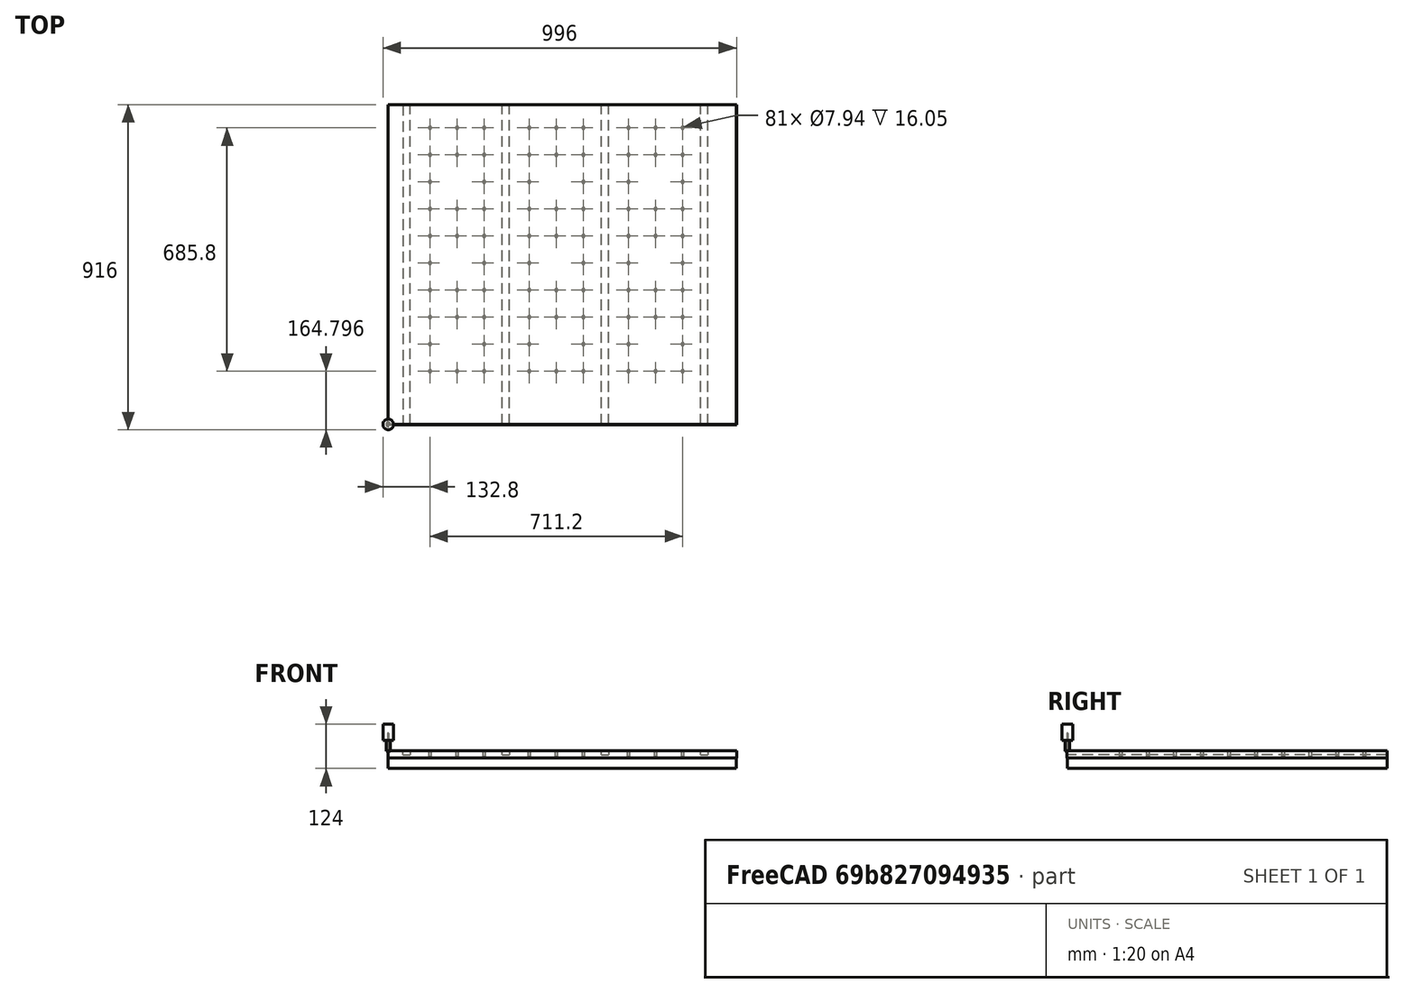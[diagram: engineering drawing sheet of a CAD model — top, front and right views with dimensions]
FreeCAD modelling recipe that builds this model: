
FCSTD DOCUMENT  (FreeCAD 0.21R33771 (Git))
Label: test
License: All rights reserved
LicenseURL: https://en.wikipedia.org/wiki/All_rights_reserved
objects: Part::FeaturePython×13, Path::FeaturePython×12, App::DocumentObjectGroup×9, Sketcher::SketchObject×3, Part::Extrusion×3, App::FeaturePython×3, Part::Cut×2, Part::Box×1, Mesh::FeaturePython×1, Part::MultiCommon×1, App::Part×1
note: 28 computed .brp shape members not serialized (recipe doc carries the construction recipe); baked Part::Feature solids carry a one-line shape summary decoded from their .brp

FEATURE [Sketcher::SketchObject] Sketch
  FullyConstrained = true
  MapMode = 5
  Placement = pos=(0,0,0) rot=(1,0,0;1.5708rad)
  Support = -> [XZ_Plane]
  sketch-geometry (8):
    g0: LineSegment StartX=0 StartY=0 StartZ=0 EndX=1219.2 EndY=0 EndZ=0
    g1: LineSegment StartX=1219.2 StartY=0 StartZ=0 EndX=1219.2 EndY=-12.7 EndZ=0
    g2: LineSegment StartX=1219.2 StartY=-12.7 StartZ=0 EndX=1193.8 EndY=-12.7 EndZ=0
    g3: LineSegment StartX=1193.8 StartY=-12.7 StartZ=0 EndX=1193.8 EndY=-19.05 EndZ=0
    g4: LineSegment StartX=1193.8 StartY=-19.05 StartZ=0 EndX=25.4 EndY=-19.05 EndZ=0
    g5: LineSegment StartX=0 StartY=0 StartZ=0 EndX=0 EndY=-12.7 EndZ=0
    g6: LineSegment StartX=0 StartY=-12.7 StartZ=0 EndX=25.4 EndY=-12.7 EndZ=0
    g7: LineSegment StartX=25.4 StartY=-19.05 StartZ=0 EndX=25.4 EndY=-12.7 EndZ=0
  constraints (23):
    c: Horizontal(g0)
    c: Coincident(g1,g0)
    c: Vertical(g1)
    c: Coincident(g2,g1)
    c: Horizontal(g2)
    c: Coincident(g3,g2)
    c: Vertical(g3)
    c: Coincident(g4,g3)
    c: Horizontal(g4)
    c: Coincident(g5,g0)
    c: Coincident(g6,g5)
    c: Horizontal(g6)
    c: Coincident(g7,g4)
    c: Coincident(g7,g6)
    c: Vertical(g7)
    c: Equal(g1,g5)
    c: Vertical(g5)
    c: Coincident(g0,g-1)
    c: DistanceX(g0,g0) = 1219.2
    c: DistanceX(g4,g4) = 1168.4
    c: DistanceY(g4,g0) = 19.05
    c: DistanceY(g5,g5) = 12.7
    c: DistanceX(g6,g6) = 25.4
FEATURE [Part::Extrusion] Extrude
  Base = -> Sketch
  Dir = (0,-1,2e-16)
  DirMode = 2
  FaceMakerClass = Part::FaceMakerBullseye
  LengthFwd = 1219.2
  LengthRev = 0
  Solid = true
  Symmetric = false
FEATURE [Sketcher::SketchObject] Sketch001
  FullyConstrained = true
  MapMode = 5
  Support = -> [Extrude]
  sketch-geometry (203):
    g0: Circle CenterX=254 CenterY=-152.4 CenterZ=0 NormalX=0 NormalY=0 NormalZ=1 AngleXU=0 Radius=3.96875
    g1: Circle CenterX=330.2 CenterY=-152.4 CenterZ=0 NormalX=0 NormalY=0 NormalZ=1 AngleXU=0 Radius=3.96875
    g2: LineSegment StartX=254 StartY=-152.4 StartZ=0 EndX=330.2 EndY=-152.4 EndZ=0
    g3: Circle CenterX=406.4 CenterY=-152.4 CenterZ=0 NormalX=0 NormalY=0 NormalZ=1 AngleXU=0 Radius=3.96875
    g4: LineSegment StartX=330.2 StartY=-152.4 StartZ=0 EndX=406.4 EndY=-152.4 EndZ=0
    g5: Circle CenterX=254 CenterY=-228.6 CenterZ=0 NormalX=0 NormalY=0 NormalZ=1 AngleXU=0 Radius=3.96875
    g6: LineSegment StartX=254 StartY=-152.4 StartZ=0 EndX=254 EndY=-228.6 EndZ=0
    g7: LineSegment StartX=254 StartY=-228.6 StartZ=0 EndX=330.2 EndY=-228.6 EndZ=0
    g8: Circle CenterX=406.4 CenterY=-228.6 CenterZ=0 NormalX=0 NormalY=0 NormalZ=1 AngleXU=0 Radius=3.96875
    g9: LineSegment StartX=330.2 StartY=-228.6 StartZ=0 EndX=406.4 EndY=-228.6 EndZ=0
    g10: Circle CenterX=254 CenterY=-304.8 CenterZ=0 NormalX=0 NormalY=0 NormalZ=1 AngleXU=0 Radius=3.96875
    g11: LineSegment StartX=254 StartY=-228.6 StartZ=0 EndX=254 EndY=-304.8 EndZ=0
    g12: Circle CenterX=330.2 CenterY=-304.8 CenterZ=0 NormalX=0 NormalY=0 NormalZ=1 AngleXU=0 Radius=3.96875
    g13: LineSegment StartX=254 StartY=-304.8 StartZ=0 EndX=330.2 EndY=-304.8 EndZ=0
    g14: Circle CenterX=406.4 CenterY=-304.8 CenterZ=0 NormalX=0 NormalY=0 NormalZ=1 AngleXU=0 Radius=3.96875
    g15: LineSegment StartX=330.2 StartY=-304.8 StartZ=0 EndX=406.4 EndY=-304.8 EndZ=0
    g16: Circle CenterX=254 CenterY=-381 CenterZ=0 NormalX=0 NormalY=0 NormalZ=1 AngleXU=0 Radius=3.96875
    g17: Circle CenterX=330.2 CenterY=-381 CenterZ=0 NormalX=0 NormalY=0 NormalZ=1 AngleXU=0 Radius=3.96875
    g18: LineSegment StartX=254 StartY=-381 StartZ=0 EndX=330.2 EndY=-381 EndZ=0
    g19: Circle CenterX=406.4 CenterY=-381 CenterZ=0 NormalX=0 NormalY=0 NormalZ=1 AngleXU=0 Radius=3.96875
    g20: LineSegment StartX=330.2 StartY=-381 StartZ=0 EndX=406.4 EndY=-381 EndZ=0
    g21: Circle CenterX=254 CenterY=-457.2 CenterZ=0 NormalX=0 NormalY=0 NormalZ=1 AngleXU=0 Radius=3.96875
    g22: LineSegment StartX=254 StartY=-381 StartZ=0 EndX=254 EndY=-457.2 EndZ=0
    g23: LineSegment StartX=254 StartY=-457.2 StartZ=0 EndX=330.2 EndY=-457.2 EndZ=0
    g24: Circle CenterX=406.4 CenterY=-457.2 CenterZ=0 NormalX=0 NormalY=0 NormalZ=1 AngleXU=0 Radius=3.96875
    g25: LineSegment StartX=330.2 StartY=-457.2 StartZ=0 EndX=406.4 EndY=-457.2 EndZ=0
    g26: Circle CenterX=254 CenterY=-533.4 CenterZ=0 NormalX=0 NormalY=0 NormalZ=1 AngleXU=0 Radius=3.96875
    g27: LineSegment StartX=254 StartY=-457.2 StartZ=0 EndX=254 EndY=-533.4 EndZ=0
    g28: Circle CenterX=330.2 CenterY=-533.4 CenterZ=0 NormalX=0 NormalY=0 NormalZ=1 AngleXU=0 Radius=3.96875
    g29: LineSegment StartX=254 StartY=-533.4 StartZ=0 EndX=330.2 EndY=-533.4 EndZ=0
    g30: Circle CenterX=406.4 CenterY=-533.4 CenterZ=0 NormalX=0 NormalY=0 NormalZ=1 AngleXU=0 Radius=3.96875
    g31: LineSegment StartX=330.2 StartY=-533.4 StartZ=0 EndX=406.4 EndY=-533.4 EndZ=0
    g32: LineSegment StartX=254 StartY=-152.4 StartZ=0 EndX=254 EndY=-381 EndZ=0
    g33: Circle CenterX=254 CenterY=-609.6 CenterZ=0 NormalX=0 NormalY=0 NormalZ=1 AngleXU=0 Radius=3.96875
    g34: Circle CenterX=330.2 CenterY=-609.6 CenterZ=0 NormalX=0 NormalY=0 NormalZ=1 AngleXU=0 Radius=3.96875
    g35: LineSegment StartX=254 StartY=-609.6 StartZ=0 EndX=330.2 EndY=-609.6 EndZ=0
    g36: Circle CenterX=406.4 CenterY=-609.6 CenterZ=0 NormalX=0 NormalY=0 NormalZ=1 AngleXU=0 Radius=3.96875
    g37: LineSegment StartX=330.2 StartY=-609.6 StartZ=0 EndX=406.4 EndY=-609.6 EndZ=0
    g38: Circle CenterX=254 CenterY=-685.8 CenterZ=0 NormalX=0 NormalY=0 NormalZ=1 AngleXU=0 Radius=3.96875
    g39: LineSegment StartX=254 StartY=-609.6 StartZ=0 EndX=254 EndY=-685.8 EndZ=0
    g40: LineSegment StartX=254 StartY=-685.8 StartZ=0 EndX=330.2 EndY=-685.8 EndZ=0
    g41: Circle CenterX=406.4 CenterY=-685.8 CenterZ=0 NormalX=0 NormalY=0 NormalZ=1 AngleXU=0 Radius=3.96875
    g42: LineSegment StartX=330.2 StartY=-685.8 StartZ=0 EndX=406.4 EndY=-685.8 EndZ=0
    g43: Circle CenterX=254 CenterY=-762 CenterZ=0 NormalX=0 NormalY=0 NormalZ=1 AngleXU=0 Radius=3.96875
    g44: LineSegment StartX=254 StartY=-685.8 StartZ=0 EndX=254 EndY=-762 EndZ=0
    g45: Circle CenterX=330.2 CenterY=-762 CenterZ=0 NormalX=0 NormalY=0 NormalZ=1 AngleXU=0 Radius=3.96875
    g46: LineSegment StartX=254 StartY=-762 StartZ=0 EndX=330.2 EndY=-762 EndZ=0
    g47: Circle CenterX=406.4 CenterY=-762 CenterZ=0 NormalX=0 NormalY=0 NormalZ=1 AngleXU=0 Radius=3.96875
    g48: LineSegment StartX=330.2 StartY=-762 StartZ=0 EndX=406.4 EndY=-762 EndZ=0
    g49: LineSegment StartX=254 StartY=-381 StartZ=0 EndX=254 EndY=-609.6 EndZ=0
    g50: Circle CenterX=254 CenterY=-838.2 CenterZ=0 NormalX=0 NormalY=0 NormalZ=1 AngleXU=0 Radius=3.96875
    g51: Circle CenterX=330.2 CenterY=-838.2 CenterZ=0 NormalX=0 NormalY=0 NormalZ=1 AngleXU=0 Radius=3.96875
    g52: LineSegment StartX=254 StartY=-838.2 StartZ=0 EndX=330.2 EndY=-838.2 EndZ=0
    g53: Circle CenterX=406.4 CenterY=-838.2 CenterZ=0 NormalX=0 NormalY=0 NormalZ=1 AngleXU=0 Radius=3.96875
    g54: LineSegment StartX=330.2 StartY=-838.2 StartZ=0 EndX=406.4 EndY=-838.2 EndZ=0
    g55: Circle CenterX=254 CenterY=-914.4 CenterZ=0 NormalX=0 NormalY=0 NormalZ=1 AngleXU=0 Radius=3.96875
    g56: LineSegment StartX=254 StartY=-838.2 StartZ=0 EndX=254 EndY=-914.4 EndZ=0
    g57: LineSegment StartX=254 StartY=-914.4 StartZ=0 EndX=330.2 EndY=-914.4 EndZ=0
    g58: Circle CenterX=406.4 CenterY=-914.4 CenterZ=0 NormalX=0 NormalY=0 NormalZ=1 AngleXU=0 Radius=3.96875
    g59: LineSegment StartX=330.2 StartY=-914.4 StartZ=0 EndX=406.4 EndY=-914.4 EndZ=0
    g60: Circle CenterX=254 CenterY=-990.6 CenterZ=0 NormalX=0 NormalY=0 NormalZ=1 AngleXU=0 Radius=3.96875
    g61: LineSegment StartX=254 StartY=-914.4 StartZ=0 EndX=254 EndY=-990.6 EndZ=0
    g62: Circle CenterX=330.2 CenterY=-990.6 CenterZ=0 NormalX=0 NormalY=0 NormalZ=1 AngleXU=0 Radius=3.96875
    g63: LineSegment StartX=254 StartY=-990.6 StartZ=0 EndX=330.2 EndY=-990.6 EndZ=0
    g64: Circle CenterX=406.4 CenterY=-990.6 CenterZ=0 NormalX=0 NormalY=0 NormalZ=1 AngleXU=0 Radius=3.96875
    g65: LineSegment StartX=330.2 StartY=-990.6 StartZ=0 EndX=406.4 EndY=-990.6 EndZ=0
    g66: LineSegment StartX=254 StartY=-609.6 StartZ=0 EndX=254 EndY=-838.2 EndZ=0
    g67: Circle CenterX=533.4 CenterY=-152.4 CenterZ=0 NormalX=0 NormalY=0 NormalZ=1 AngleXU=0 Radius=3.96875
    g68: Circle CenterX=609.6 CenterY=-152.4 CenterZ=0 NormalX=0 NormalY=0 NormalZ=1 AngleXU=0 Radius=3.96875
    g69: LineSegment StartX=533.4 StartY=-152.4 StartZ=0 EndX=609.6 EndY=-152.4 EndZ=0
    g70: Circle CenterX=685.8 CenterY=-152.4 CenterZ=0 NormalX=0 NormalY=0 NormalZ=1 AngleXU=0 Radius=3.96875
    g71: LineSegment StartX=609.6 StartY=-152.4 StartZ=0 EndX=685.8 EndY=-152.4 EndZ=0
    g72: Circle CenterX=533.4 CenterY=-228.6 CenterZ=0 NormalX=0 NormalY=0 NormalZ=1 AngleXU=0 Radius=3.96875
    g73: LineSegment StartX=533.4 StartY=-152.4 StartZ=0 EndX=533.4 EndY=-228.6 EndZ=0
    g74: LineSegment StartX=533.4 StartY=-228.6 StartZ=0 EndX=609.6 EndY=-228.6 EndZ=0
    g75: Circle CenterX=685.8 CenterY=-228.6 CenterZ=0 NormalX=0 NormalY=0 NormalZ=1 AngleXU=0 Radius=3.96875
    g76: LineSegment StartX=609.6 StartY=-228.6 StartZ=0 EndX=685.8 EndY=-228.6 EndZ=0
    g77: Circle CenterX=533.4 CenterY=-304.8 CenterZ=0 NormalX=0 NormalY=0 NormalZ=1 AngleXU=0 Radius=3.96875
    g78: LineSegment StartX=533.4 StartY=-228.6 StartZ=0 EndX=533.4 EndY=-304.8 EndZ=0
    g79: Circle CenterX=609.6 CenterY=-304.8 CenterZ=0 NormalX=0 NormalY=0 NormalZ=1 AngleXU=0 Radius=3.96875
    g80: LineSegment StartX=533.4 StartY=-304.8 StartZ=0 EndX=609.6 EndY=-304.8 EndZ=0
    g81: Circle CenterX=685.8 CenterY=-304.8 CenterZ=0 NormalX=0 NormalY=0 NormalZ=1 AngleXU=0 Radius=3.96875
    g82: LineSegment StartX=609.6 StartY=-304.8 StartZ=0 EndX=685.8 EndY=-304.8 EndZ=0
    g83: Circle CenterX=533.4 CenterY=-381 CenterZ=0 NormalX=0 NormalY=0 NormalZ=1 AngleXU=0 Radius=3.96875
    g84: Circle CenterX=609.6 CenterY=-381 CenterZ=0 NormalX=0 NormalY=0 NormalZ=1 AngleXU=0 Radius=3.96875
    g85: LineSegment StartX=533.4 StartY=-381 StartZ=0 EndX=609.6 EndY=-381 EndZ=0
    g86: Circle CenterX=685.8 CenterY=-381 CenterZ=0 NormalX=0 NormalY=0 NormalZ=1 AngleXU=0 Radius=3.96875
    g87: LineSegment StartX=609.6 StartY=-381 StartZ=0 EndX=685.8 EndY=-381 EndZ=0
    g88: Circle CenterX=533.4 CenterY=-457.2 CenterZ=0 NormalX=0 NormalY=0 NormalZ=1 AngleXU=0 Radius=3.96875
    g89: LineSegment StartX=533.4 StartY=-381 StartZ=0 EndX=533.4 EndY=-457.2 EndZ=0
    g90: LineSegment StartX=533.4 StartY=-457.2 StartZ=0 EndX=609.6 EndY=-457.2 EndZ=0
    g91: Circle CenterX=685.8 CenterY=-457.2 CenterZ=0 NormalX=0 NormalY=0 NormalZ=1 AngleXU=0 Radius=3.96875
    g92: LineSegment StartX=609.6 StartY=-457.2 StartZ=0 EndX=685.8 EndY=-457.2 EndZ=0
    g93: Circle CenterX=533.4 CenterY=-533.4 CenterZ=0 NormalX=0 NormalY=0 NormalZ=1 AngleXU=0 Radius=3.96875
    g94: LineSegment StartX=533.4 StartY=-457.2 StartZ=0 EndX=533.4 EndY=-533.4 EndZ=0
    g95: Circle CenterX=609.6 CenterY=-533.4 CenterZ=0 NormalX=0 NormalY=0 NormalZ=1 AngleXU=0 Radius=3.96875
    g96: LineSegment StartX=533.4 StartY=-533.4 StartZ=0 EndX=609.6 EndY=-533.4 EndZ=0
    g97: Circle CenterX=685.8 CenterY=-533.4 CenterZ=0 NormalX=0 NormalY=0 NormalZ=1 AngleXU=0 Radius=3.96875
    g98: LineSegment StartX=609.6 StartY=-533.4 StartZ=0 EndX=685.8 EndY=-533.4 EndZ=0
    g99: LineSegment StartX=533.4 StartY=-152.4 StartZ=0 EndX=533.4 EndY=-381 EndZ=0
    g100: Circle CenterX=533.4 CenterY=-609.6 CenterZ=0 NormalX=0 NormalY=0 NormalZ=1 AngleXU=0 Radius=3.96875
    g101: Circle CenterX=609.6 CenterY=-609.6 CenterZ=0 NormalX=0 NormalY=0 NormalZ=1 AngleXU=0 Radius=3.96875
    g102: LineSegment StartX=533.4 StartY=-609.6 StartZ=0 EndX=609.6 EndY=-609.6 EndZ=0
    g103: Circle CenterX=685.8 CenterY=-609.6 CenterZ=0 NormalX=0 NormalY=0 NormalZ=1 AngleXU=0 Radius=3.96875
    g104: LineSegment StartX=609.6 StartY=-609.6 StartZ=0 EndX=685.8 EndY=-609.6 EndZ=0
    g105: Circle CenterX=533.4 CenterY=-685.8 CenterZ=0 NormalX=0 NormalY=0 NormalZ=1 AngleXU=0 Radius=3.96875
    g106: LineSegment StartX=533.4 StartY=-609.6 StartZ=0 EndX=533.4 EndY=-685.8 EndZ=0
    g107: LineSegment StartX=533.4 StartY=-685.8 StartZ=0 EndX=609.6 EndY=-685.8 EndZ=0
    g108: Circle CenterX=685.8 CenterY=-685.8 CenterZ=0 NormalX=0 NormalY=0 NormalZ=1 AngleXU=0 Radius=3.96875
    g109: LineSegment StartX=609.6 StartY=-685.8 StartZ=0 EndX=685.8 EndY=-685.8 EndZ=0
    g110: Circle CenterX=533.4 CenterY=-762 CenterZ=0 NormalX=0 NormalY=0 NormalZ=1 AngleXU=0 Radius=3.96875
    g111: LineSegment StartX=533.4 StartY=-685.8 StartZ=0 EndX=533.4 EndY=-762 EndZ=0
    g112: Circle CenterX=609.6 CenterY=-762 CenterZ=0 NormalX=0 NormalY=0 NormalZ=1 AngleXU=0 Radius=3.96875
    g113: LineSegment StartX=533.4 StartY=-762 StartZ=0 EndX=609.6 EndY=-762 EndZ=0
    g114: Circle CenterX=685.8 CenterY=-762 CenterZ=0 NormalX=0 NormalY=0 NormalZ=1 AngleXU=0 Radius=3.96875
    g115: LineSegment StartX=609.6 StartY=-762 StartZ=0 EndX=685.8 EndY=-762 EndZ=0
    g116: LineSegment StartX=533.4 StartY=-381 StartZ=0 EndX=533.4 EndY=-609.6 EndZ=0
    g117: Circle CenterX=533.4 CenterY=-838.2 CenterZ=0 NormalX=0 NormalY=0 NormalZ=1 AngleXU=0 Radius=3.96875
    g118: Circle CenterX=609.6 CenterY=-838.2 CenterZ=0 NormalX=0 NormalY=0 NormalZ=1 AngleXU=0 Radius=3.96875
    g119: LineSegment StartX=533.4 StartY=-838.2 StartZ=0 EndX=609.6 EndY=-838.2 EndZ=0
    g120: Circle CenterX=685.8 CenterY=-838.2 CenterZ=0 NormalX=0 NormalY=0 NormalZ=1 AngleXU=0 Radius=3.96875
    g121: LineSegment StartX=609.6 StartY=-838.2 StartZ=0 EndX=685.8 EndY=-838.2 EndZ=0
    g122: Circle CenterX=533.4 CenterY=-914.4 CenterZ=0 NormalX=0 NormalY=0 NormalZ=1 AngleXU=0 Radius=3.96875
    g123: LineSegment StartX=533.4 StartY=-838.2 StartZ=0 EndX=533.4 EndY=-914.4 EndZ=0
    g124: LineSegment StartX=533.4 StartY=-914.4 StartZ=0 EndX=609.6 EndY=-914.4 EndZ=0
    g125: Circle CenterX=685.8 CenterY=-914.4 CenterZ=0 NormalX=0 NormalY=0 NormalZ=1 AngleXU=0 Radius=3.96875
    g126: LineSegment StartX=609.6 StartY=-914.4 StartZ=0 EndX=685.8 EndY=-914.4 EndZ=0
    g127: Circle CenterX=533.4 CenterY=-990.6 CenterZ=0 NormalX=0 NormalY=0 NormalZ=1 AngleXU=0 Radius=3.96875
    g128: LineSegment StartX=533.4 StartY=-914.4 StartZ=0 EndX=533.4 EndY=-990.6 EndZ=0
    g129: Circle CenterX=609.6 CenterY=-990.6 CenterZ=0 NormalX=0 NormalY=0 NormalZ=1 AngleXU=0 Radius=3.96875
    g130: LineSegment StartX=533.4 StartY=-990.6 StartZ=0 EndX=609.6 EndY=-990.6 EndZ=0
    g131: Circle CenterX=685.8 CenterY=-990.6 CenterZ=0 NormalX=0 NormalY=0 NormalZ=1 AngleXU=0 Radius=3.96875
    g132: LineSegment StartX=609.6 StartY=-990.6 StartZ=0 EndX=685.8 EndY=-990.6 EndZ=0
    g133: LineSegment StartX=533.4 StartY=-609.6 StartZ=0 EndX=533.4 EndY=-838.2 EndZ=0
    g134: LineSegment StartX=254 StartY=-152.4 StartZ=0 EndX=533.4 EndY=-152.4 EndZ=0
    g135: Circle CenterX=812.8 CenterY=-152.4 CenterZ=0 NormalX=0 NormalY=0 NormalZ=1 AngleXU=0 Radius=3.96875
    g136: Circle CenterX=889 CenterY=-152.4 CenterZ=0 NormalX=0 NormalY=0 NormalZ=1 AngleXU=0 Radius=3.96875
    g137: LineSegment StartX=812.8 StartY=-152.4 StartZ=0 EndX=889 EndY=-152.4 EndZ=0
    g138: Circle CenterX=965.2 CenterY=-152.4 CenterZ=0 NormalX=0 NormalY=0 NormalZ=1 AngleXU=0 Radius=3.96875
    g139: LineSegment StartX=889 StartY=-152.4 StartZ=0 EndX=965.2 EndY=-152.4 EndZ=0
    g140: Circle CenterX=812.8 CenterY=-228.6 CenterZ=0 NormalX=0 NormalY=0 NormalZ=1 AngleXU=0 Radius=3.96875
    g141: LineSegment StartX=812.8 StartY=-152.4 StartZ=0 EndX=812.8 EndY=-228.6 EndZ=0
    g142: LineSegment StartX=812.8 StartY=-228.6 StartZ=0 EndX=889 EndY=-228.6 EndZ=0
    g143: Circle CenterX=965.2 CenterY=-228.6 CenterZ=0 NormalX=0 NormalY=0 NormalZ=1 AngleXU=0 Radius=3.96875
    g144: LineSegment StartX=889 StartY=-228.6 StartZ=0 EndX=965.2 EndY=-228.6 EndZ=0
    g145: Circle CenterX=812.8 CenterY=-304.8 CenterZ=0 NormalX=0 NormalY=0 NormalZ=1 AngleXU=0 Radius=3.96875
    g146: LineSegment StartX=812.8 StartY=-228.6 StartZ=0 EndX=812.8 EndY=-304.8 EndZ=0
    g147: Circle CenterX=889 CenterY=-304.8 CenterZ=0 NormalX=0 NormalY=0 NormalZ=1 AngleXU=0 Radius=3.96875
    g148: LineSegment StartX=812.8 StartY=-304.8 StartZ=0 EndX=889 EndY=-304.8 EndZ=0
    g149: Circle CenterX=965.2 CenterY=-304.8 CenterZ=0 NormalX=0 NormalY=0 NormalZ=1 AngleXU=0 Radius=3.96875
    g150: LineSegment StartX=889 StartY=-304.8 StartZ=0 EndX=965.2 EndY=-304.8 EndZ=0
    g151: Circle CenterX=812.8 CenterY=-381 CenterZ=0 NormalX=0 NormalY=0 NormalZ=1 AngleXU=0 Radius=3.96875
    g152: Circle CenterX=889 CenterY=-381 CenterZ=0 NormalX=0 NormalY=0 NormalZ=1 AngleXU=0 Radius=3.96875
    g153: LineSegment StartX=812.8 StartY=-381 StartZ=0 EndX=889 EndY=-381 EndZ=0
    g154: Circle CenterX=965.2 CenterY=-381 CenterZ=0 NormalX=0 NormalY=0 NormalZ=1 AngleXU=0 Radius=3.96875
    g155: LineSegment StartX=889 StartY=-381 StartZ=0 EndX=965.2 EndY=-381 EndZ=0
    g156: Circle CenterX=812.8 CenterY=-457.2 CenterZ=0 NormalX=0 NormalY=0 NormalZ=1 AngleXU=0 Radius=3.96875
    g157: LineSegment StartX=812.8 StartY=-381 StartZ=0 EndX=812.8 EndY=-457.2 EndZ=0
    g158: LineSegment StartX=812.8 StartY=-457.2 StartZ=0 EndX=889 EndY=-457.2 EndZ=0
    g159: Circle CenterX=965.2 CenterY=-457.2 CenterZ=0 NormalX=0 NormalY=0 NormalZ=1 AngleXU=0 Radius=3.96875
    g160: LineSegment StartX=889 StartY=-457.2 StartZ=0 EndX=965.2 EndY=-457.2 EndZ=0
    g161: Circle CenterX=812.8 CenterY=-533.4 CenterZ=0 NormalX=0 NormalY=0 NormalZ=1 AngleXU=0 Radius=3.96875
    g162: LineSegment StartX=812.8 StartY=-457.2 StartZ=0 EndX=812.8 EndY=-533.4 EndZ=0
    g163: Circle CenterX=889 CenterY=-533.4 CenterZ=0 NormalX=0 NormalY=0 NormalZ=1 AngleXU=0 Radius=3.96875
    g164: LineSegment StartX=812.8 StartY=-533.4 StartZ=0 EndX=889 EndY=-533.4 EndZ=0
    g165: Circle CenterX=965.2 CenterY=-533.4 CenterZ=0 NormalX=0 NormalY=0 NormalZ=1 AngleXU=0 Radius=3.96875
    g166: LineSegment StartX=889 StartY=-533.4 StartZ=0 EndX=965.2 EndY=-533.4 EndZ=0
    g167: LineSegment StartX=812.8 StartY=-152.4 StartZ=0 EndX=812.8 EndY=-381 EndZ=0
    g168: Circle CenterX=812.8 CenterY=-609.6 CenterZ=0 NormalX=0 NormalY=0 NormalZ=1 AngleXU=0 Radius=3.96875
    g169: Circle CenterX=889 CenterY=-609.6 CenterZ=0 NormalX=0 NormalY=0 NormalZ=1 AngleXU=0 Radius=3.96875
    g170: LineSegment StartX=812.8 StartY=-609.6 StartZ=0 EndX=889 EndY=-609.6 EndZ=0
    g171: Circle CenterX=965.2 CenterY=-609.6 CenterZ=0 NormalX=0 NormalY=0 NormalZ=1 AngleXU=0 Radius=3.96875
    g172: LineSegment StartX=889 StartY=-609.6 StartZ=0 EndX=965.2 EndY=-609.6 EndZ=0
    g173: Circle CenterX=812.8 CenterY=-685.8 CenterZ=0 NormalX=0 NormalY=0 NormalZ=1 AngleXU=0 Radius=3.96875
    g174: LineSegment StartX=812.8 StartY=-609.6 StartZ=0 EndX=812.8 EndY=-685.8 EndZ=0
    g175: LineSegment StartX=812.8 StartY=-685.8 StartZ=0 EndX=889 EndY=-685.8 EndZ=0
    g176: Circle CenterX=965.2 CenterY=-685.8 CenterZ=0 NormalX=0 NormalY=0 NormalZ=1 AngleXU=0 Radius=3.96875
    g177: LineSegment StartX=889 StartY=-685.8 StartZ=0 EndX=965.2 EndY=-685.8 EndZ=0
    g178: Circle CenterX=812.8 CenterY=-762 CenterZ=0 NormalX=0 NormalY=0 NormalZ=1 AngleXU=0 Radius=3.96875
    g179: LineSegment StartX=812.8 StartY=-685.8 StartZ=0 EndX=812.8 EndY=-762 EndZ=0
    g180: Circle CenterX=889 CenterY=-762 CenterZ=0 NormalX=0 NormalY=0 NormalZ=1 AngleXU=0 Radius=3.96875
    g181: LineSegment StartX=812.8 StartY=-762 StartZ=0 EndX=889 EndY=-762 EndZ=0
    g182: Circle CenterX=965.2 CenterY=-762 CenterZ=0 NormalX=0 NormalY=0 NormalZ=1 AngleXU=0 Radius=3.96875
    g183: LineSegment StartX=889 StartY=-762 StartZ=0 EndX=965.2 EndY=-762 EndZ=0
    g184: LineSegment StartX=812.8 StartY=-381 StartZ=0 EndX=812.8 EndY=-609.6 EndZ=0
    g185: Circle CenterX=812.8 CenterY=-838.2 CenterZ=0 NormalX=0 NormalY=0 NormalZ=1 AngleXU=0 Radius=3.96875
    g186: Circle CenterX=889 CenterY=-838.2 CenterZ=0 NormalX=0 NormalY=0 NormalZ=1 AngleXU=0 Radius=3.96875
    g187: LineSegment StartX=812.8 StartY=-838.2 StartZ=0 EndX=889 EndY=-838.2 EndZ=0
    g188: Circle CenterX=965.2 CenterY=-838.2 CenterZ=0 NormalX=0 NormalY=0 NormalZ=1 AngleXU=0 Radius=3.96875
    g189: LineSegment StartX=889 StartY=-838.2 StartZ=0 EndX=965.2 EndY=-838.2 EndZ=0
    g190: Circle CenterX=812.8 CenterY=-914.4 CenterZ=0 NormalX=0 NormalY=0 NormalZ=1 AngleXU=0 Radius=3.96875
    g191: LineSegment StartX=812.8 StartY=-838.2 StartZ=0 EndX=812.8 EndY=-914.4 EndZ=0
    g192: LineSegment StartX=812.8 StartY=-914.4 StartZ=0 EndX=889 EndY=-914.4 EndZ=0
    g193: Circle CenterX=965.2 CenterY=-914.4 CenterZ=0 NormalX=0 NormalY=0 NormalZ=1 AngleXU=0 Radius=3.96875
    g194: LineSegment StartX=889 StartY=-914.4 StartZ=0 EndX=965.2 EndY=-914.4 EndZ=0
    g195: Circle CenterX=812.8 CenterY=-990.6 CenterZ=0 NormalX=0 NormalY=0 NormalZ=1 AngleXU=0 Radius=3.96875
    g196: LineSegment StartX=812.8 StartY=-914.4 StartZ=0 EndX=812.8 EndY=-990.6 EndZ=0
    g197: Circle CenterX=889 CenterY=-990.6 CenterZ=0 NormalX=0 NormalY=0 NormalZ=1 AngleXU=0 Radius=3.96875
    g198: LineSegment StartX=812.8 StartY=-990.6 StartZ=0 EndX=889 EndY=-990.6 EndZ=0
    g199: Circle CenterX=965.2 CenterY=-990.6 CenterZ=0 NormalX=0 NormalY=0 NormalZ=1 AngleXU=0 Radius=3.96875
    g200: LineSegment StartX=889 StartY=-990.6 StartZ=0 EndX=965.2 EndY=-990.6 EndZ=0
    g201: LineSegment StartX=812.8 StartY=-609.6 StartZ=0 EndX=812.8 EndY=-838.2 EndZ=0
    g202: LineSegment StartX=533.4 StartY=-152.4 StartZ=0 EndX=812.8 EndY=-152.4 EndZ=0
  constraints (514):
    c: Diameter(g0) = 7.9375
    c: DistanceY(g0,g-1) = 152.4
    c: DistanceX(g-1,g0) = 254
    c: Equal(g0,g1) = 7.9375
    c: Coincident(g0,g2)
    c: Coincident(g1,g2)
    c: Distance(g2) = 76.2
    c: Angle(g2) = 0
    c: Equal(g0,g3) = 7.9375
    c: Coincident(g1,g4)
    c: Coincident(g3,g4)
    c: Equal(g2,g4)
    c: Parallel(g4,g2)
    c: Equal(g0,g5) = 7.9375
    c: Coincident(g0,g6)
    c: Coincident(g5,g6)
    c: Equal(g6,g2)
    c: Perpendicular(g6,g2)
    c: Coincident(g5,g7)
    c: Equal(g2,g7)
    c: Parallel(g7,g2)
    c: Equal(g0,g8) = 7.9375
    c: Coincident(g8,g9)
    c: Equal(g2,g9)
    c: Parallel(g9,g2)
    c: Equal(g0,g10) = 7.9375
    c: Coincident(g5,g11)
    c: Coincident(g10,g11)
    c: Equal(g6,g11)
    c: Perpendicular(g11,g2)
    c: Equal(g0,g12) = 7.9375
    c: Coincident(g10,g13)
    c: Coincident(g12,g13)
    c: Equal(g2,g13)
    c: Parallel(g13,g2)
    c: Equal(g0,g14) = 7.9375
    c: Coincident(g12,g15)
    c: Coincident(g14,g15)
    c: Equal(g2,g15)
    c: Parallel(g15,g2)
    c: Coincident(g9,g7)
    c: Equal(g0,g16) = 7.9375
    c: Equal(g16,g17) = 7.9375
    c: Coincident(g16,g18)
    c: Coincident(g17,g18)
    c: Equal(g2,g18) = 76.2
    c: Parallel(g2,g18)
    c: Equal(g16,g19) = 7.9375
    c: Coincident(g17,g20)
    c: Coincident(g19,g20)
    c: Equal(g18,g20)
    c: Parallel(g20,g18)
    c: Equal(g16,g21) = 7.9375
    c: Coincident(g16,g22)
    c: Coincident(g21,g22)
    c: Equal(g22,g18)
    c: Perpendicular(g22,g18)
    c: Coincident(g21,g23)
    c: Equal(g18,g23)
    c: Parallel(g23,g18)
    c: Equal(g16,g24) = 7.9375
    c: Coincident(g24,g25)
    c: Equal(g18,g25)
    c: Parallel(g25,g18)
    c: Equal(g16,g26) = 7.9375
    c: Coincident(g21,g27)
    c: Coincident(g26,g27)
    c: Equal(g22,g27)
    c: Perpendicular(g27,g18)
    c: Equal(g16,g28) = 7.9375
    c: Coincident(g26,g29)
    c: Coincident(g28,g29)
    c: Equal(g18,g29)
    c: Parallel(g29,g18)
    c: Equal(g16,g30) = 7.9375
    c: Coincident(g28,g31)
    c: Coincident(g30,g31)
    c: Equal(g18,g31)
    c: Parallel(g31,g18)
    c: Coincident(g25,g23)
    c: Coincident(g0,g32)
    c: Coincident(g16,g32)
    c: Distance(g32) = 228.6
    c: Angle(g32) = -1.5708
    c: Equal(g0,g33) = 7.9375
    c: Equal(g33,g34) = 7.9375
    c: Coincident(g33,g35)
    c: Coincident(g34,g35)
    c: Equal(g2,g35) = 76.2
    c: Parallel(g2,g35)
    c: Equal(g33,g36) = 7.9375
    c: Coincident(g34,g37)
    c: Coincident(g36,g37)
    c: Equal(g35,g37)
    c: Parallel(g37,g35)
    c: Equal(g33,g38) = 7.9375
    c: Coincident(g33,g39)
    c: Coincident(g38,g39)
    c: Equal(g39,g35)
    c: Perpendicular(g39,g35)
    c: Coincident(g38,g40)
    c: Equal(g35,g40)
    c: Parallel(g40,g35)
    c: Equal(g33,g41) = 7.9375
    c: Coincident(g41,g42)
    c: Equal(g35,g42)
    c: Parallel(g42,g35)
    c: Equal(g33,g43) = 7.9375
    c: Coincident(g38,g44)
    c: Coincident(g43,g44)
    c: Equal(g39,g44)
    c: Perpendicular(g44,g35)
    c: Equal(g33,g45) = 7.9375
    c: Coincident(g43,g46)
    c: Coincident(g45,g46)
    c: Equal(g35,g46)
    c: Parallel(g46,g35)
    c: Equal(g33,g47) = 7.9375
    c: Coincident(g45,g48)
    c: Coincident(g47,g48)
    c: Equal(g35,g48)
    c: Parallel(g48,g35)
    c: Coincident(g42,g40)
    c: Coincident(g16,g49)
    c: Coincident(g33,g49)
    c: Equal(g32,g49)
    c: Parallel(g49,g32)
    c: Equal(g0,g50) = 7.9375
    c: Equal(g50,g51) = 7.9375
    c: Coincident(g50,g52)
    c: Coincident(g51,g52)
    c: Equal(g2,g52) = 76.2
    c: Parallel(g2,g52)
    c: Equal(g50,g53) = 7.9375
    c: Coincident(g51,g54)
    c: Coincident(g53,g54)
    c: Equal(g52,g54)
    c: Parallel(g54,g52)
    c: Equal(g50,g55) = 7.9375
    c: Coincident(g50,g56)
    c: Coincident(g55,g56)
    c: Equal(g56,g52)
    c: Perpendicular(g56,g52)
    c: Coincident(g55,g57)
    c: Equal(g52,g57)
    c: Parallel(g57,g52)
    c: Equal(g50,g58) = 7.9375
    c: Coincident(g58,g59)
    c: Equal(g52,g59)
    c: Parallel(g59,g52)
    c: Equal(g50,g60) = 7.9375
    c: Coincident(g55,g61)
    c: Coincident(g60,g61)
    c: Equal(g56,g61)
    c: Perpendicular(g61,g52)
    c: Equal(g50,g62) = 7.9375
    c: Coincident(g60,g63)
    c: Coincident(g62,g63)
    c: Equal(g52,g63)
    c: Parallel(g63,g52)
    c: Equal(g50,g64) = 7.9375
    c: Coincident(g62,g65)
    c: Coincident(g64,g65)
    c: Equal(g52,g65)
    c: Parallel(g65,g52)
    c: Coincident(g59,g57)
    c: Coincident(g33,g66)
    c: Coincident(g50,g66)
    c: Equal(g32,g66)
    c: Parallel(g66,g32)
    c: Equal(g0,g67) = 7.9375
    c: Equal(g67,g68) = 7.9375
    c: Coincident(g67,g69)
    c: Coincident(g68,g69)
    c: Equal(g2,g69) = 76.2
    c: Parallel(g2,g69)
    c: Equal(g67,g70) = 7.9375
    c: Coincident(g68,g71)
    c: Coincident(g70,g71)
    c: Equal(g69,g71)
    c: Parallel(g71,g69)
    c: Equal(g67,g72) = 7.9375
    c: Coincident(g67,g73)
    c: Coincident(g72,g73)
    c: Equal(g73,g69)
    c: Perpendicular(g73,g69)
    c: Coincident(g72,g74)
    c: Equal(g69,g74)
    c: Parallel(g74,g69)
    c: Equal(g67,g75) = 7.9375
    c: Coincident(g75,g76)
    c: Equal(g69,g76)
    c: Parallel(g76,g69)
    c: Equal(g67,g77) = 7.9375
    c: Coincident(g72,g78)
    c: Coincident(g77,g78)
    c: Equal(g73,g78)
    c: Perpendicular(g78,g69)
    c: Equal(g67,g79) = 7.9375
    c: Coincident(g77,g80)
    c: Coincident(g79,g80)
    c: Equal(g69,g80)
    c: Parallel(g80,g69)
    c: Equal(g67,g81) = 7.9375
    c: Coincident(g79,g82)
    c: Coincident(g81,g82)
    c: Equal(g69,g82)
    c: Parallel(g82,g69)
    c: Coincident(g76,g74)
    c: Equal(g67,g83) = 7.9375
    c: Equal(g83,g84) = 7.9375
    c: Coincident(g83,g85)
    c: Coincident(g84,g85)
    c: Equal(g69,g85) = 76.2
    c: Parallel(g69,g85)
    c: Equal(g83,g86) = 7.9375
    c: Coincident(g84,g87)
    c: Coincident(g86,g87)
    c: Equal(g85,g87)
    c: Parallel(g87,g85)
    c: Equal(g83,g88) = 7.9375
    c: Coincident(g83,g89)
    c: Coincident(g88,g89)
    c: Equal(g89,g85)
    c: Perpendicular(g89,g85)
    c: Coincident(g88,g90)
    c: Equal(g85,g90)
    c: Parallel(g90,g85)
    c: Equal(g83,g91) = 7.9375
    c: Coincident(g91,g92)
    c: Equal(g85,g92)
    c: Parallel(g92,g85)
    c: Equal(g83,g93) = 7.9375
    c: Coincident(g88,g94)
    c: Coincident(g93,g94)
    c: Equal(g89,g94)
    c: Perpendicular(g94,g85)
    c: Equal(g83,g95) = 7.9375
    c: Coincident(g93,g96)
    c: Coincident(g95,g96)
    c: Equal(g85,g96)
    c: Parallel(g96,g85)
    c: Equal(g83,g97) = 7.9375
    c: Coincident(g95,g98)
    c: Coincident(g97,g98)
    c: Equal(g85,g98)
    c: Parallel(g98,g85)
    c: Coincident(g92,g90)
    c: Coincident(g67,g99)
    c: Coincident(g83,g99)
    c: Equal(g32,g99) = 228.6
    c: Parallel(g32,g99) = -1.5708
    c: Equal(g67,g100) = 7.9375
    c: Equal(g100,g101) = 7.9375
    c: Coincident(g100,g102)
    c: Coincident(g101,g102)
    c: Equal(g69,g102) = 76.2
    c: Parallel(g69,g102)
    c: Equal(g100,g103) = 7.9375
    c: Coincident(g101,g104)
    c: Coincident(g103,g104)
    c: Equal(g102,g104)
    c: Parallel(g104,g102)
    c: Equal(g100,g105) = 7.9375
    c: Coincident(g100,g106)
    c: Coincident(g105,g106)
    c: Equal(g106,g102)
    c: Perpendicular(g106,g102)
    c: Coincident(g105,g107)
    c: Equal(g102,g107)
    c: Parallel(g107,g102)
    c: Equal(g100,g108) = 7.9375
    c: Coincident(g108,g109)
    c: Equal(g102,g109)
    c: Parallel(g109,g102)
    c: Equal(g100,g110) = 7.9375
    c: Coincident(g105,g111)
    c: Coincident(g110,g111)
    c: Equal(g106,g111)
    c: Perpendicular(g111,g102)
    c: Equal(g100,g112) = 7.9375
    c: Coincident(g110,g113)
    c: Coincident(g112,g113)
    c: Equal(g102,g113)
    c: Parallel(g113,g102)
    c: Equal(g100,g114) = 7.9375
    c: Coincident(g112,g115)
    c: Coincident(g114,g115)
    c: Equal(g102,g115)
    c: Parallel(g115,g102)
    c: Coincident(g109,g107)
    c: Coincident(g83,g116)
    c: Coincident(g100,g116)
    c: Equal(g99,g116)
    c: Parallel(g116,g99)
    c: Equal(g67,g117) = 7.9375
    c: Equal(g117,g118) = 7.9375
    c: Coincident(g117,g119)
    c: Coincident(g118,g119)
    c: Equal(g69,g119) = 76.2
    c: Parallel(g69,g119)
    c: Equal(g117,g120) = 7.9375
    c: Coincident(g118,g121)
    c: Coincident(g120,g121)
    c: Equal(g119,g121)
    c: Parallel(g121,g119)
    c: Equal(g117,g122) = 7.9375
    c: Coincident(g117,g123)
    c: Coincident(g122,g123)
    c: Equal(g123,g119)
    c: Perpendicular(g123,g119)
    c: Coincident(g122,g124)
    c: Equal(g119,g124)
    c: Parallel(g124,g119)
    c: Equal(g117,g125) = 7.9375
    c: Coincident(g125,g126)
    c: Equal(g119,g126)
    c: Parallel(g126,g119)
    c: Equal(g117,g127) = 7.9375
    c: Coincident(g122,g128)
    c: Coincident(g127,g128)
    c: Equal(g123,g128)
    c: Perpendicular(g128,g119)
    c: Equal(g117,g129) = 7.9375
    c: Coincident(g127,g130)
    c: Coincident(g129,g130)
    c: Equal(g119,g130)
    c: Parallel(g130,g119)
    c: Equal(g117,g131) = 7.9375
    c: Coincident(g129,g132)
    c: Coincident(g131,g132)
    c: Equal(g119,g132)
    c: Parallel(g132,g119)
    c: Coincident(g126,g124)
    c: Coincident(g100,g133)
    c: Coincident(g117,g133)
    c: Equal(g99,g133)
    c: Parallel(g133,g99)
    c: Coincident(g0,g134)
    c: Coincident(g67,g134)
    c: Distance(g134) = 279.4
    c: Angle(g134) = 0
    c: Equal(g0,g135) = 7.9375
    c: Equal(g135,g136) = 7.9375
    c: Coincident(g135,g137)
    c: Coincident(g136,g137)
    c: Equal(g2,g137) = 76.2
    c: Parallel(g2,g137)
    c: Equal(g135,g138) = 7.9375
    c: Coincident(g136,g139)
    c: Coincident(g138,g139)
    c: Equal(g137,g139)
    c: Parallel(g139,g137)
    c: Equal(g135,g140) = 7.9375
    c: Coincident(g135,g141)
    c: Coincident(g140,g141)
    c: Equal(g141,g137)
    c: Perpendicular(g141,g137)
    c: Coincident(g140,g142)
    c: Equal(g137,g142)
    c: Parallel(g142,g137)
    c: Equal(g135,g143) = 7.9375
    c: Coincident(g143,g144)
    c: Equal(g137,g144)
    c: Parallel(g144,g137)
    c: Equal(g135,g145) = 7.9375
    c: Coincident(g140,g146)
    c: Coincident(g145,g146)
    c: Equal(g141,g146)
    c: Perpendicular(g146,g137)
    c: Equal(g135,g147) = 7.9375
    c: Coincident(g145,g148)
    c: Coincident(g147,g148)
    c: Equal(g137,g148)
    c: Parallel(g148,g137)
    c: Equal(g135,g149) = 7.9375
    c: Coincident(g147,g150)
    c: Coincident(g149,g150)
    c: Equal(g137,g150)
    c: Parallel(g150,g137)
    c: Coincident(g144,g142)
    c: Equal(g135,g151) = 7.9375
    c: Equal(g151,g152) = 7.9375
    c: Coincident(g151,g153)
    c: Coincident(g152,g153)
    c: Equal(g137,g153) = 76.2
    c: Parallel(g137,g153)
    c: Equal(g151,g154) = 7.9375
    c: Coincident(g152,g155)
    c: Coincident(g154,g155)
    c: Equal(g153,g155)
    c: Parallel(g155,g153)
    c: Equal(g151,g156) = 7.9375
    c: Coincident(g151,g157)
    c: Coincident(g156,g157)
    c: Equal(g157,g153)
    c: Perpendicular(g157,g153)
    c: Coincident(g156,g158)
    c: Equal(g153,g158)
    c: Parallel(g158,g153)
    c: Equal(g151,g159) = 7.9375
    c: Coincident(g159,g160)
    c: Equal(g153,g160)
    c: Parallel(g160,g153)
    c: Equal(g151,g161) = 7.9375
    c: Coincident(g156,g162)
    c: Coincident(g161,g162)
    c: Equal(g157,g162)
    c: Perpendicular(g162,g153)
    c: Equal(g151,g163) = 7.9375
    c: Coincident(g161,g164)
    c: Coincident(g163,g164)
    c: Equal(g153,g164)
    c: Parallel(g164,g153)
    c: Equal(g151,g165) = 7.9375
    c: Coincident(g163,g166)
    c: Coincident(g165,g166)
    c: Equal(g153,g166)
    c: Parallel(g166,g153)
    c: Coincident(g160,g158)
    c: Coincident(g135,g167)
    c: Coincident(g151,g167)
    c: Equal(g32,g167) = 228.6
    c: Parallel(g32,g167) = -1.5708
    c: Equal(g135,g168) = 7.9375
    c: Equal(g168,g169) = 7.9375
    c: Coincident(g168,g170)
    c: Coincident(g169,g170)
    c: Equal(g137,g170) = 76.2
    c: Parallel(g137,g170)
    c: Equal(g168,g171) = 7.9375
    c: Coincident(g169,g172)
    c: Coincident(g171,g172)
    c: Equal(g170,g172)
    c: Parallel(g172,g170)
    c: Equal(g168,g173) = 7.9375
    c: Coincident(g168,g174)
    c: Coincident(g173,g174)
    c: Equal(g174,g170)
    c: Perpendicular(g174,g170)
    c: Coincident(g173,g175)
    c: Equal(g170,g175)
    c: Parallel(g175,g170)
    c: Equal(g168,g176) = 7.9375
    c: Coincident(g176,g177)
    c: Equal(g170,g177)
    c: Parallel(g177,g170)
    c: Equal(g168,g178) = 7.9375
    c: Coincident(g173,g179)
    c: Coincident(g178,g179)
    c: Equal(g174,g179)
    c: Perpendicular(g179,g170)
    c: Equal(g168,g180) = 7.9375
    c: Coincident(g178,g181)
    c: Coincident(g180,g181)
    c: Equal(g170,g181)
    c: Parallel(g181,g170)
    c: Equal(g168,g182) = 7.9375
    c: Coincident(g180,g183)
    c: Coincident(g182,g183)
    c: Equal(g170,g183)
    c: Parallel(g183,g170)
    c: Coincident(g177,g175)
    c: Coincident(g151,g184)
    c: Coincident(g168,g184)
    c: Equal(g167,g184)
    c: Parallel(g184,g167)
    c: Equal(g135,g185) = 7.9375
    c: Equal(g185,g186) = 7.9375
    c: Coincident(g185,g187)
    c: Coincident(g186,g187)
    c: Equal(g137,g187) = 76.2
    c: Parallel(g137,g187)
    c: Equal(g185,g188) = 7.9375
    c: Coincident(g186,g189)
    c: Coincident(g188,g189)
    c: Equal(g187,g189)
    c: Parallel(g189,g187)
    c: Equal(g185,g190) = 7.9375
    c: Coincident(g185,g191)
    c: Coincident(g190,g191)
    c: Equal(g191,g187)
    c: Perpendicular(g191,g187)
    c: Coincident(g190,g192)
    c: Equal(g187,g192)
    c: Parallel(g192,g187)
    c: Equal(g185,g193) = 7.9375
    c: Coincident(g193,g194)
    c: Equal(g187,g194)
    c: Parallel(g194,g187)
    c: Equal(g185,g195) = 7.9375
    c: Coincident(g190,g196)
    c: Coincident(g195,g196)
    c: Equal(g191,g196)
    c: Perpendicular(g196,g187)
    c: Equal(g185,g197) = 7.9375
    c: Coincident(g195,g198)
    c: Coincident(g197,g198)
    c: Equal(g187,g198)
    c: Parallel(g198,g187)
    c: Equal(g185,g199) = 7.9375
    c: Coincident(g197,g200)
    c: Coincident(g199,g200)
    c: Equal(g187,g200)
    c: Parallel(g200,g187)
    c: Coincident(g194,g192)
    c: Coincident(g168,g201)
    c: Coincident(g185,g201)
    c: Equal(g167,g201)
    c: Parallel(g201,g167)
    c: Coincident(g67,g202)
    c: Coincident(g135,g202)
    c: Equal(g134,g202)
    c: Parallel(g202,g134)
FEATURE [Part::Extrusion] Extrude001
  Base = -> Sketch001
  Dir = (0,2e-16,1)
  DirMode = 2
  FaceMakerClass = Part::FaceMakerBullseye
  LengthFwd = 19.05
  LengthRev = 16.05
  Solid = true
  Symmetric = false
FEATURE [Part::Cut] Cut
  Base = -> Extrude
  Tool = -> Extrude001
FEATURE [Sketcher::SketchObject] Sketch002
  FullyConstrained = true
  MapMode = 5
  Support = -> [Cut]
  sketch-geometry (19):
    g0: LineSegment StartX=177.8 StartY=25.4 StartZ=0 EndX=197.85 EndY=25.4 EndZ=0
    g1: LineSegment StartX=197.85 StartY=25.4 StartZ=0 EndX=197.85 EndY=-1244.6 EndZ=0
    g2: LineSegment StartX=197.85 StartY=-1244.6 StartZ=0 EndX=177.8 EndY=-1244.6 EndZ=0
    g3: LineSegment StartX=177.8 StartY=-1244.6 StartZ=0 EndX=177.8 EndY=25.4 EndZ=0
    g4: LineSegment StartX=457.2 StartY=25.4 StartZ=0 EndX=477.25 EndY=25.4 EndZ=0
    g5: LineSegment StartX=477.25 StartY=25.4 StartZ=0 EndX=477.25 EndY=-1244.6 EndZ=0
    g6: LineSegment StartX=477.25 StartY=-1244.6 StartZ=0 EndX=457.2 EndY=-1244.6 EndZ=0
    g7: LineSegment StartX=457.2 StartY=-1244.6 StartZ=0 EndX=457.2 EndY=25.4 EndZ=0
    g8: LineSegment StartX=177.8 StartY=25.4 StartZ=0 EndX=457.2 EndY=25.4 EndZ=0
    g9: LineSegment StartX=736.6 StartY=25.4 StartZ=0 EndX=756.65 EndY=25.4 EndZ=0
    g10: LineSegment StartX=756.65 StartY=25.4 StartZ=0 EndX=756.65 EndY=-1244.6 EndZ=0
    g11: LineSegment StartX=756.65 StartY=-1244.6 StartZ=0 EndX=736.6 EndY=-1244.6 EndZ=0
    g12: LineSegment StartX=736.6 StartY=-1244.6 StartZ=0 EndX=736.6 EndY=25.4 EndZ=0
    g13: LineSegment StartX=457.2 StartY=25.4 StartZ=0 EndX=736.6 EndY=25.4 EndZ=0
    g14: LineSegment StartX=1016 StartY=25.4 StartZ=0 EndX=1036.05 EndY=25.4 EndZ=0
    g15: LineSegment StartX=1036.05 StartY=25.4 StartZ=0 EndX=1036.05 EndY=-1244.6 EndZ=0
    g16: LineSegment StartX=1036.05 StartY=-1244.6 StartZ=0 EndX=1016 EndY=-1244.6 EndZ=0
    g17: LineSegment StartX=1016 StartY=-1244.6 StartZ=0 EndX=1016 EndY=25.4 EndZ=0
    g18: LineSegment StartX=736.6 StartY=25.4 StartZ=0 EndX=1016 EndY=25.4 EndZ=0
  constraints (54):
    c: Coincident(g0,g1)
    c: Coincident(g1,g2)
    c: Coincident(g2,g3)
    c: Coincident(g3,g0)
    c: Horizontal(g0)
    c: Horizontal(g2)
    c: Vertical(g1)
    c: Vertical(g3)
    c: DistanceY(g-1,g0) = 25.4
    c: DistanceY(g3,g3) = 1270
    c: DistanceX(g0,g0) = 20.05
    c: DistanceX(g-1,g0) = 177.8
    c: Coincident(g4,g5)
    c: Coincident(g5,g6)
    c: Coincident(g6,g7)
    c: Coincident(g7,g4)
    c: Horizontal(g4)
    c: Horizontal(g6)
    c: Vertical(g5)
    c: Vertical(g7)
    c: Equal(g3,g7) = 1270
    c: Equal(g0,g4) = 25.4
    c: Coincident(g0,g8)
    c: Coincident(g4,g8)
    c: Distance(g8) = 279.4
    c: Angle(g8) = 0
    c: Coincident(g9,g10)
    c: Coincident(g10,g11)
    c: Coincident(g11,g12)
    c: Coincident(g12,g9)
    c: Horizontal(g9)
    c: Horizontal(g11)
    c: Vertical(g10)
    c: Vertical(g12)
    c: Equal(g3,g12) = 1270
    c: Equal(g0,g9) = 25.4
    c: Coincident(g4,g13)
    c: Coincident(g9,g13)
    c: Equal(g8,g13)
    c: Parallel(g13,g8)
    c: Coincident(g14,g15)
    c: Coincident(g15,g16)
    c: Coincident(g16,g17)
    c: Coincident(g17,g14)
    c: Horizontal(g14)
    c: Horizontal(g16)
    c: Vertical(g15)
    c: Vertical(g17)
    c: Equal(g3,g17) = 1270
    c: Equal(g0,g14) = 25.4
    c: Coincident(g9,g18)
    c: Coincident(g14,g18)
    c: Equal(g8,g18)
    c: Parallel(g18,g8)
FEATURE [Part::Extrusion] Extrude002
  Base = -> Sketch002
  Dir = (0,2e-16,1)
  DirMode = 2
  FaceMakerClass = Part::FaceMakerBullseye
  LengthFwd = 12.7
  LengthRev = 10.525
  Solid = true
  Symmetric = false
FEATURE [Part::Cut] Cut001
  Base = -> Cut
  Placement = pos=(-136.2,1140.4,0) rot=(0,0,1;0rad)
  Tool = -> Extrude002
FEATURE [Part::Box] Box  label="Cube"
  AttacherType = Attacher::AttachEngine3D
  Height = 50
  Length = 980
  Placement = pos=(0,0,-49) rot=(0,0,1;0rad)
  Width = 900
FEATURE [App::FeaturePython] SetupSheet  # Path/CAM operation (typed FeaturePython)
  ClearanceHeightExpression = OpStockZMax+SetupSheet.ClearanceHeightOffset
  ClearanceHeightOffset = 5
  CoolantMode = 0
  CoolantModes = None | Flood | Mist
  FinalDepthExpression = OpFinalDepth
  HorizRapid = 0
  SafeHeightExpression = OpStockZMax+SetupSheet.SafeHeightOffset
  SafeHeightOffset = 3
  StartDepthExpression = OpStartDepth
  StepDownExpression = OpToolDiameter
  VertRapid = 0
FEATURE [Part::FeaturePython] ToolBit  label="Endmill"  # Path/CAM toolbit (typed FeaturePython)
  BitPropertyNames = Chipload | CuttingEdgeHeight | Diameter | Flutes | Length | Material | ShankDiameter | SpindleDirection
  BitShape = <path>
  Chipload = 0
  CuttingEdgeHeight = 30
  Diameter = 5
  Flutes = 0
  Length = 50
  Material = 0
  ShankDiameter = 3
  ShapeName = endmill
  SpindleDirection = 0
FEATURE [Part::FeaturePython] ToolBit002  label="6mm_Endmill"  # Path/CAM toolbit (typed FeaturePython)
  BitPropertyNames = Chipload | CuttingEdgeHeight | Diameter | Flutes | Length | Material | ShankDiameter | SpindleDirection
  BitShape = <path>
  Chipload = 0
  CuttingEdgeHeight = 30
  Diameter = 6
  File = <userpath>/AppData/Roaming/FreeCAD/Macro\Bit\6mm_Endmill.fctb
  Flutes = 0
  Length = 50
  Material = 0
  ShankDiameter = 3
  ShapeName = endmill
  SpindleDirection = 0
FEATURE [Path::FeaturePython] TC__6mm_Endmill  label="TC: 6mm_Endmill"  # Path/CAM operation (typed FeaturePython)
  HorizFeed = 20
  HorizRapid = 0
  SpindleDir = 0
  SpindleSpeed = 0
  Tool = -> ToolBit002
  ToolNumber = 1
  VertFeed = 20
  VertRapid = 0
  expr: HorizRapid = SetupSheet.HorizRapid
  expr: VertRapid = SetupSheet.VertRapid
FEATURE [Mesh::FeaturePython] CutMaterial  # WARN: FeaturePython — macro-defined, semantics opaque (R4)
FEATURE [Part::MultiCommon] Common
  Shapes = -> [Box,Cut001]
FEATURE [App::Part] Part
  Group = -> [Box,Cut,Cut001,Extrude001,Extrude,Extrude002,Sketch,Sketch001,Sketch002,Common]
  Origin = -> Origin
FEATURE [Part::FeaturePython] Clone  label="Model-Part"  # Draft clone (typed FeaturePython)
  AttacherType = Attacher::AttachEngine3D
  Fuse = false
  Objects = -> [Part]
  PathResource = Model
  Scale = (1,1,1)
FEATURE [App::DocumentObjectGroup] Model
  Group = -> [Clone]
FEATURE [App::FeaturePython] SetupSheet001  # Path/CAM operation (typed FeaturePython)
  ClearanceHeightExpression = OpStockZMax+SetupSheet001.ClearanceHeightOffset
  ClearanceHeightOffset = 5
  CoolantMode = 0
  CoolantModes = None | Flood | Mist
  FinalDepthExpression = OpFinalDepth
  HorizRapid = 0
  SafeHeightExpression = OpStockZMax+SetupSheet001.SafeHeightOffset
  SafeHeightOffset = 3
  StartDepthExpression = OpStartDepth
  StepDownExpression = OpToolDiameter
  VertRapid = 0
FEATURE [Part::FeaturePython] Clone043  label="Model-Part001"  # Draft clone (typed FeaturePython)
  AttacherType = Attacher::AttachEngine3D
  Fuse = false
  Objects = -> [Part]
  PathResource = Model
  Scale = (1,1,1)
FEATURE [App::DocumentObjectGroup] Model001
  Group = -> [Clone043]
FEATURE [Part::FeaturePython] Stock  # WARN: FeaturePython — macro-defined, semantics opaque (R4)
  Base = -> Model001
  ExtXneg = 1
  ExtXpos = 1
  ExtYneg = 1
  ExtYpos = 1
  ExtZneg = 1
  ExtZpos = 1
  Placement = pos=(0,0,-19.05) rot=(0,0,1;0rad)
  StockType = FromBase
FEATURE [Part::FeaturePython] ToolBit004  label="6mm_Endmill001"  # Path/CAM toolbit (typed FeaturePython)
  BitPropertyNames = Chipload | CuttingEdgeHeight | Diameter | Flutes | Length | Material | ShankDiameter | SpindleDirection
  BitShape = <path>
  Chipload = 0
  CuttingEdgeHeight = 30
  Diameter = 6
  File = <userpath>/AppData/Roaming/FreeCAD/Macro/Bit/6mm_Endmill.fctb
  Flutes = 0
  Length = 50
  Material = 0
  ShankDiameter = 3
  ShapeName = endmill
  SpindleDirection = 0
FEATURE [Path::FeaturePython] _mm_Endmill001  label="6mm_Endmill002"  # Path/CAM operation (typed FeaturePython)
  HorizFeed = 12.5
  HorizRapid = 0
  SpindleDir = 0
  SpindleSpeed = 0
  Tool = -> ToolBit004
  ToolNumber = 2
  VertFeed = 8.33333
  VertRapid = 0
  expr: HorizRapid = SetupSheet001.HorizRapid
  expr: VertRapid = SetupSheet001.VertRapid
FEATURE [App::DocumentObjectGroup] Tools001
  Group = -> [_mm_Endmill001]
FEATURE [Path::FeaturePython] Pocket_Shape001  # Path/CAM operation (typed FeaturePython)
  Active = true
  AreaParams:
    Tolerance = 1e-07
    FitArcs = True
    Simplify = False
    CleanDistance = 0.0
    Accuracy = 0.01
    Unit = 1.0
    MinArcPoints = 4
    MaxArcPoints = 100
    ClipperScale = 10000000.0
    Fill = 0
    Coplanar = 0
    Reorient = True
    Outline = False
    Explode = False
    OpenMode = 0
    Deflection = 0.01
    SubjectFill = 0
    ClipFill = 0
    Offset = 0.0
    ExtraPass = 0
    Stepover = 0.0
    LastStepover = 0.0
    JoinType = 0
    EndType = 0
    MiterLimit = 2.0
    RoundPrecision = 0.0
    PocketMode = 5
    ToolRadius = 3.0
    PocketExtraOffset = 0.0
    PocketStepover = 6.0
    PocketLastStepover = 0.0
    FromCenter = True
    Angle = 90.0
    AngleShift = 0.0
    Shift = 0.0
    Thicken = False
    SectionCount = -1
    Stepdown = 1.0
    SectionOffset = 0.0
    SectionTolerance = 1e-07
    SectionMode = 2
    Project = False
  Base = -> [Clone]
  ClearanceHeight = 6
  CoolantMode = 0
  CutMode = 0
  CycleTime = 00:13:23
  ExtensionCorners = true
  ExtensionLengthDefault = 3
  ExtraOffset = 0
  FinalDepth = -10.525
  FinishDepth = 0
  KeepToolDown = false
  MinTravel = false
  OffsetPattern = 3
  OpFinalDepth = -10.525
  OpStartDepth = 1
  OpStockZMax = 1
  OpStockZMin = -20.05
  OpToolDiameter = 6
  PathParams = {'orientation': 1, 'feedrate': 12.5, 'feedrate_v': 8.333333333333334, 'verbose': True, 'resume_height': 4.000000000000252, 'retraction': 6.000000000000252, 'return_end': True, 'preamble': False, 'start': Vector (616.5366534999999, 897.0, 6.000000000000252)}
  PocketLastStepOver = 0
  SafeHeight = 4
  SplitArcs = false
  StartAt = 0
  StartDepth = 1
  StartPoint = (0,0,0)
  StepDown = 15
  StepOver = 100
  ToolController = -> _mm_Endmill001
  UseOutline = false
  UseStartPoint = false
  ZigZagAngle = 90
  expr: ClearanceHeight = OpStockZMax + SetupSheet001.ClearanceHeightOffset
  expr: ExtensionLengthDefault = OpToolDiameter / 2
  expr: FinalDepth = OpFinalDepth
  expr: SafeHeight = OpStockZMax + SetupSheet001.SafeHeightOffset
  expr: StartDepth = OpStartDepth
  expr: StepDown = 15
FEATURE [App::DocumentObjectGroup] Operations001
  Group = -> [Pocket_Shape001]
FEATURE [Path::FeaturePython] Job001  # Path/CAM operation (typed FeaturePython)
  CycleTime = 00:13:23
  Fixtures = G54
  GeometryTolerance = 0.01
  JobType = 0
  LastPostProcessDate = 2024-05-05 21:45:26.869749
  LastPostProcessOutput = <userpath>/Desktop/CNC_Project/CAM/surfacing3.nc
  Model = -> Model001
  Operations = -> Operations001
  OrderOutputBy = 0
  PostProcessor = 13
  PostProcessorOutputFile = <userpath>/Desktop/CNC_Project/CAM/surfacing3.nc
  SetupSheet = -> SetupSheet001
  SplitOutput = false
  Stock = -> Stock
  Tools = -> Tools001
FEATURE [App::FeaturePython] SetupSheet002  # Path/CAM operation (typed FeaturePython)
  ClearanceHeightExpression = OpStockZMax+SetupSheet002.ClearanceHeightOffset
  ClearanceHeightOffset = 5
  CoolantMode = 0
  CoolantModes = None | Flood | Mist
  FinalDepthExpression = OpFinalDepth
  HorizRapid = 0
  SafeHeightExpression = OpStockZMax+SetupSheet002.SafeHeightOffset
  SafeHeightOffset = 3
  StartDepthExpression = OpStartDepth
  StepDownExpression = OpToolDiameter
  VertRapid = 0
FEATURE [Part::FeaturePython] Clone076  label="Model-Part002"  # Draft clone (typed FeaturePython)
  AttacherType = Attacher::AttachEngine3D
  Fuse = false
  Objects = -> [Part]
  PathResource = Model
  Scale = (1,1,1)
FEATURE [App::DocumentObjectGroup] Model002
  Group = -> [Clone076]
FEATURE [Part::FeaturePython] ToolBit005  label="Endmill001"  # Path/CAM toolbit (typed FeaturePython)
  BitPropertyNames = Chipload | CuttingEdgeHeight | Diameter | Flutes | Length | Material | ShankDiameter | SpindleDirection
  BitShape = <path>
  Chipload = 0
  CuttingEdgeHeight = 30
  Diameter = 5
  Flutes = 0
  Length = 50
  Material = 0
  ShankDiameter = 3
  ShapeName = endmill
  SpindleDirection = 0
FEATURE [Part::FeaturePython] Stock001  # WARN: FeaturePython — macro-defined, semantics opaque (R4)
  Base = -> Model002
  ExtXneg = 1
  ExtXpos = 1
  ExtYneg = 1
  ExtYpos = 1
  ExtZneg = 1
  ExtZpos = 1
  Placement = pos=(0,0,-19.05) rot=(0,0,1;0rad)
  StockType = FromBase
FEATURE [Part::FeaturePython] ToolBit006  label="Endmill004"  # Path/CAM toolbit (typed FeaturePython)
  BitPropertyNames = Chipload | CuttingEdgeHeight | Diameter | Flutes | Length | Material | ShankDiameter | SpindleDirection
  BitShape = <path>
  Chipload = 0
  CuttingEdgeHeight = 30
  Diameter = 5
  Flutes = 0
  Length = 50
  Material = 0
  ShankDiameter = 3
  ShapeName = endmill
  SpindleDirection = 0
FEATURE [Part::FeaturePython] ToolBit008  label="12mm_Endmill"  # Path/CAM toolbit (typed FeaturePython)
  BitPropertyNames = Chipload | CuttingEdgeHeight | Diameter | Flutes | Length | Material | ShankDiameter | SpindleDirection
  BitShape = <path>
  Chipload = 0
  CuttingEdgeHeight = 30
  Diameter = 12
  File = <userpath>/.local/share/FreeCAD/Macro/Bit/12mm_Endmill.fctb
  Flutes = 0
  Length = 75
  Material = 0
  ShankDiameter = 30
  ShapeName = endmill
  SpindleDirection = 0
FEATURE [Path::FeaturePython] TC__12mm_Endmill  label="TC: 12mm_Endmill"  # Path/CAM operation (typed FeaturePython)
  HorizFeed = 0
  HorizRapid = 0
  SpindleDir = 0
  SpindleSpeed = 0
  Tool = -> ToolBit008
  ToolNumber = 10
  VertFeed = 0
  VertRapid = 0
  expr: HorizRapid = SetupSheet.HorizRapid
  expr: VertRapid = SetupSheet.VertRapid
FEATURE [App::DocumentObjectGroup] Tools
  Group = -> [TC__6mm_Endmill,TC__12mm_Endmill]
FEATURE [Part::FeaturePython] ToolBit009  label="12mm_Endmill001"  # Path/CAM toolbit (typed FeaturePython)
  BitPropertyNames = Chipload | CuttingEdgeHeight | Diameter | Flutes | Length | Material | ShankDiameter | SpindleDirection
  BitShape = <path>
  Chipload = 0
  CuttingEdgeHeight = 30
  Diameter = 12
  File = <userpath>/.local/share/FreeCAD/Macro/Bit/12mm_Endmill.fctb
  Flutes = 0
  Length = 75
  Material = 0
  ShankDiameter = 30
  ShapeName = endmill
  SpindleDirection = 0
FEATURE [Path::FeaturePython] TC__12mm_Endmill001  label="TC: 12mm_Endmill001"  # Path/CAM operation (typed FeaturePython)
  HorizFeed = 16.6667
  HorizRapid = 0
  SpindleDir = 0
  SpindleSpeed = 0
  Tool = -> ToolBit009
  ToolNumber = 1
  VertFeed = 8.33333
  VertRapid = 0
  expr: HorizRapid = SetupSheet002.HorizRapid
  expr: VertRapid = SetupSheet002.VertRapid
FEATURE [App::DocumentObjectGroup] Tools002
  Group = -> [TC__12mm_Endmill001]
FEATURE [Path::FeaturePython] MillFace  # Path/CAM operation (typed FeaturePython)
  Active = true
  BoundaryShape = 0
  ClearEdges = false
  ClearanceHeight = 0
  CoolantMode = 0
  CutMode = 0
  ExcludeRaisedAreas = false
  ExtraOffset = 0
  FinalDepth = 0
  FinishDepth = 0
  KeepToolDown = false
  MinTravel = false
  OffsetPattern = 0
  OpFinalDepth = 0
  OpStartDepth = 0
  OpStockZMax = 0
  OpStockZMin = 0
  OpToolDiameter = 0
  PocketLastStepOver = 0
  SafeHeight = 0
  SplitArcs = false
  StartAt = 0
  StartDepth = 0
  StartPoint = (0,0,0)
  StepDown = 0
  StepOver = 0
  UseStartPoint = false
  ZigZagAngle = 0
FEATURE [Part::FeaturePython] Clone075  label="Stock-Cube"  # Draft clone (typed FeaturePython)
  AttacherType = Attacher::AttachEngine3D
  Fuse = false
  Objects = -> [Box]
  PathResource = Stock
  Placement = pos=(0,0,-49) rot=(0,0,1;0rad)
  Scale = (1,1,1)
  StockType = Unknown
FEATURE [Path::FeaturePython] Pocket_Shape  # Path/CAM operation (typed FeaturePython)
  Active = true
  AreaParams:
    Tolerance = 1e-07
    FitArcs = True
    Simplify = False
    CleanDistance = 0.0
    Accuracy = 0.01
    Unit = 1.0
    MinArcPoints = 4
    MaxArcPoints = 100
    ClipperScale = 10000000.0
    Fill = 0
    Coplanar = 0
    Reorient = True
    Outline = False
    Explode = False
    OpenMode = 0
    Deflection = 0.01
    SubjectFill = 0
    ClipFill = 0
    Offset = 0.0
    ExtraPass = 0
    Stepover = 0.0
    LastStepover = 0.0
    JoinType = 0
    EndType = 0
    MiterLimit = 2.0
    RoundPrecision = 0.0
    PocketMode = 1
    ToolRadius = 3.0
    PocketExtraOffset = 0.0
    PocketStepover = 6.0
    PocketLastStepover = 0.0
    FromCenter = True
    Angle = 45.0
    AngleShift = 0.0
    Shift = 0.0
    Thicken = False
    SectionCount = -1
    Stepdown = 1.0
    SectionOffset = 0.0
    SectionTolerance = 1e-07
    SectionMode = 2
    Project = False
  Base = -> [Clone]
  ClearanceHeight = 6
  CoolantMode = 0
  CutMode = 0
  CycleTime = 00:10:51
  ExtensionCorners = true
  ExtensionLengthDefault = 3
  ExtraOffset = 0
  FinalDepth = -10.525
  FinishDepth = 0
  KeepToolDown = false
  MinTravel = false
  OffsetPattern = 0
  OpFinalDepth = -10.525
  OpStartDepth = 1
  OpStockZMax = 1
  OpStockZMin = -49
  OpToolDiameter = 6
  PathParams = {'orientation': 1, 'feedrate': 20.0, 'feedrate_v': 20.0, 'verbose': True, 'resume_height': 4.0, 'retraction': 6.0, 'return_end': True, 'preamble': False, 'start': Vector (603.5248930008665, 896.9999999428845, 6.0)}
  PocketLastStepOver = 0
  SafeHeight = 4
  SplitArcs = false
  StartAt = 0
  StartDepth = 1
  StartPoint = (0,0,0)
  StepDown = 15
  StepOver = 100
  ToolController = -> TC__6mm_Endmill
  UseOutline = false
  UseStartPoint = true
  ZigZagAngle = 45
  expr: ClearanceHeight = OpStockZMax + SetupSheet.ClearanceHeightOffset
  expr: ExtensionLengthDefault = OpToolDiameter / 2
  expr: FinalDepth = OpFinalDepth
  expr: SafeHeight = OpStockZMax + SetupSheet.SafeHeightOffset
  expr: StartDepth = OpStartDepth
  expr: StepDown = 15
FEATURE [Path::FeaturePython] Profile  # Path/CAM operation (typed FeaturePython)
  Active = true
  AreaParams:
    Tolerance = 1e-07
    FitArcs = True
    Simplify = False
    CleanDistance = 0.0
    Accuracy = 0.01
    Unit = 1.0
    MinArcPoints = 4
    MaxArcPoints = 100
    ClipperScale = 10000000.0
    Fill = 0
    Coplanar = 0
    Reorient = True
    Outline = False
    Explode = False
    OpenMode = 0
    Deflection = 0.01
    SubjectFill = 0
    ClipFill = 0
    Offset = -3.0
    ExtraPass = 0
    Stepover = 0.0
    LastStepover = 0.0
    JoinType = 0
    EndType = 0
    MiterLimit = 2.0
    RoundPrecision = 0.0
    PocketMode = 0
    ToolRadius = 1.0
    PocketExtraOffset = 0.0
    PocketStepover = 0.0
    PocketLastStepover = 0.0
    FromCenter = False
    Angle = 45.0
    AngleShift = 0.0
    Shift = 0.0
    Thicken = False
    SectionCount = -1
    Stepdown = 1.0
    SectionOffset = 0.0
    SectionTolerance = 1e-07
    SectionMode = 2
    Project = False
  Base = -> [Clone]
  ClearanceHeight = 6
  CoolantMode = 0
  CycleTime = 00:14:43
  Direction = 0
  FinalDepth = -10.525
  HandleMultipleFeatures = 0
  JoinType = 0
  MiterLimit = 0.1
  OffsetExtra = 0
  OpFinalDepth = -10.525
  OpStartDepth = 1
  OpStockZMax = 1
  OpStockZMin = -49
  OpToolDiameter = 6
  PathParams = {'orientation': 1, 'feedrate': 20.0, 'feedrate_v': 20.0, 'verbose': True, 'resume_height': 4.0, 'retraction': 6.0, 'return_end': True, 'preamble': False}
  SafeHeight = 4
  Side = 1
  SplitArcs = false
  StartDepth = 1
  StartPoint = (0,0,0)
  StepDown = 6
  ToolController = -> TC__6mm_Endmill
  UseComp = true
  UseStartPoint = false
  processCircles = false
  processHoles = false
  processPerimeter = true
  expr: ClearanceHeight = OpStockZMax + SetupSheet.ClearanceHeightOffset
  expr: FinalDepth = OpFinalDepth
  expr: SafeHeight = OpStockZMax + SetupSheet.SafeHeightOffset
  expr: StartDepth = OpStartDepth
  expr: StepDown = OpToolDiameter
FEATURE [App::DocumentObjectGroup] Operations
  Group = -> [Pocket_Shape,Profile]
FEATURE [Path::FeaturePython] Job  # Path/CAM operation (typed FeaturePython)
  CycleTime = 00:25:34
  Fixtures = G54
  GeometryTolerance = 0.01
  JobType = 0
  LastPostProcessDate = 2024-05-06 20:39:23.332026
  LastPostProcessOutput = <userpath>/Desktop/CNC_Project/CAM/pocketing7.nc
  Model = -> Model
  Operations = -> Operations
  OrderOutputBy = 0
  PostProcessor = 13
  PostProcessorOutputFile = <userpath>/Desktop/CNC_Project/CAM/pocketing7.nc
  SetupSheet = -> SetupSheet
  SplitOutput = false
  Stock = -> Clone075
  Tools = -> Tools
FEATURE [Path::FeaturePython] MillFace001  # Path/CAM operation (typed FeaturePython)
  Active = true
  AreaParams:
    Tolerance = 1e-07
    FitArcs = True
    Simplify = False
    CleanDistance = 0.0
    Accuracy = 0.01
    Unit = 1.0
    MinArcPoints = 4
    MaxArcPoints = 100
    ClipperScale = 10000000.0
    Fill = 0
    Coplanar = 0
    Reorient = True
    Outline = False
    Explode = False
    OpenMode = 0
    Deflection = 0.01
    SubjectFill = 0
    ClipFill = 0
    Offset = 0.0
    ExtraPass = 0
    Stepover = 0.0
    LastStepover = 0.0
    JoinType = 0
    EndType = 0
    MiterLimit = 2.0
    RoundPrecision = 0.0
    PocketMode = 1
    ToolRadius = 6.0
    PocketExtraOffset = 0.0
    PocketStepover = 6.0
    PocketLastStepover = 0.0
    FromCenter = True
    Angle = 45.0
    AngleShift = 0.0
    Shift = 0.0
    Thicken = False
    SectionCount = -1
    Stepdown = 1.0
    SectionOffset = 0.0
    SectionTolerance = 1e-07
    SectionMode = 2
    Project = False
  Base = -> [Clone076]
  BoundaryShape = 3
  ClearEdges = true
  ClearanceHeight = 6
  CoolantMode = 0
  CutMode = 0
  CycleTime = 02:26:40
  ExcludeRaisedAreas = false
  ExtraOffset = 0
  FinalDepth = 2.51e-13
  FinishDepth = 0
  KeepToolDown = false
  MinTravel = true
  OffsetPattern = 0
  OpFinalDepth = 2.51e-13
  OpStartDepth = 1
  OpStockZMax = 1
  OpStockZMin = -20.05
  OpToolDiameter = 12
  PathParams = {'orientation': 1, 'sort_mode': 3, 'threshold': 12.0, 'feedrate': 16.666666666666668, 'feedrate_v': 8.333333333333334, 'verbose': True, 'resume_height': 4.000000000000252, 'retraction': 6.000000000000252, 'return_end': True, 'preamble': False, 'start': Vector (0.0, 0.0, 0.0)}
  PocketLastStepOver = 0
  SafeHeight = 4
  SplitArcs = false
  StartAt = 0
  StartDepth = 1
  StartPoint = (0,0,0)
  StepDown = 12
  StepOver = 50
  ToolController = -> TC__12mm_Endmill001
  UseStartPoint = true
  ZigZagAngle = 45
  expr: ClearanceHeight = OpStockZMax + SetupSheet002.ClearanceHeightOffset
  expr: FinalDepth = OpFinalDepth
  expr: SafeHeight = OpStockZMax + SetupSheet002.SafeHeightOffset
  expr: StartDepth = OpStartDepth
  expr: StepDown = OpToolDiameter
FEATURE [App::DocumentObjectGroup] Operations002
  Group = -> [MillFace001]
FEATURE [Path::FeaturePython] Job002  # Path/CAM operation (typed FeaturePython)
  CycleTime = 02:26:40
  Fixtures = G54
  GeometryTolerance = 0.01
  JobType = 0
  LastPostProcessDate = 2024-05-06 22:12:21.329938
  LastPostProcessOutput = <userpath>/Desktop/CNC_Project/CAM/surfacing4.nc
  Model = -> Model002
  Operations = -> Operations002
  OrderOutputBy = 0
  PostProcessor = 13
  PostProcessorOutputFile = <userpath>/Desktop/CNC_Project/CAM/surfacing4.nc
  SetupSheet = -> SetupSheet002
  SplitOutput = false
  Stock = -> Stock001
  Tools = -> Tools002
note: 7 file-system paths scrubbed to <path> (originals preserved in the JSON sidecar)
